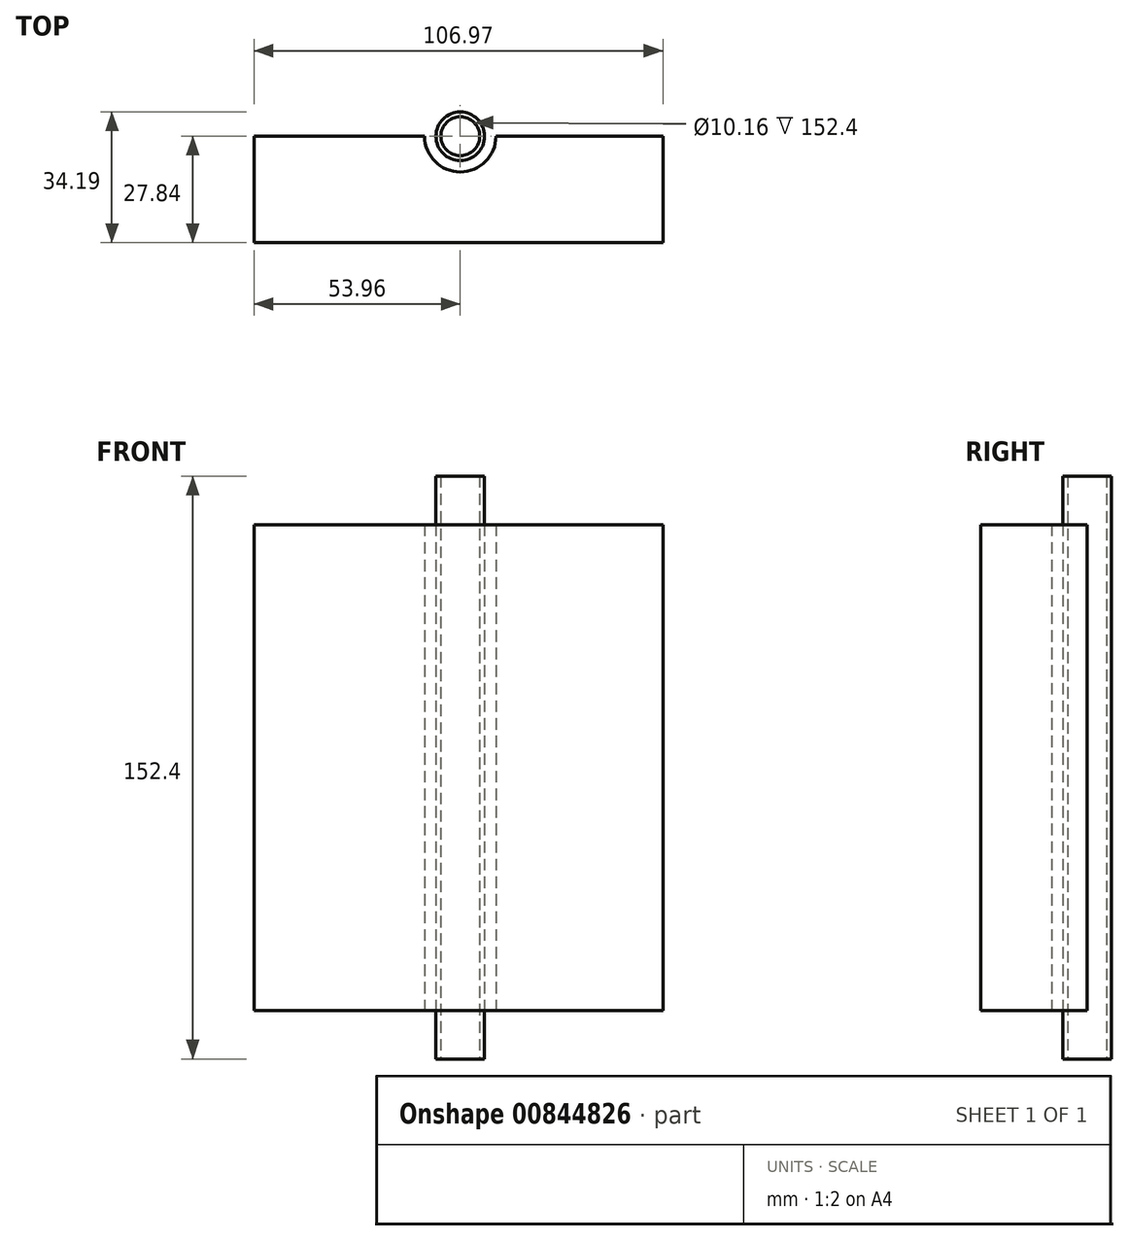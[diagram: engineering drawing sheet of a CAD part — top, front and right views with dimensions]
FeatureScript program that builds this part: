
annotation { "Feature Type Name" : "Feature", "Feature Type Description" : "" }
export const myFeature = defineFeature(function(context is Context, id is Id, definition is map)
    precondition{}
    {
        {
            var Q0;
            Q0=qCreatedBy(makeId("Top.planeOp"),FACE);
            var sketch = newSketch(context, id + "F0", { "sketchPlane" : qUnion([Q0])});
            skCircle(sketch, "E0", {"center": v(0, 0) * mm, "radius": 5.08 * mm});
            skCircle(sketch, "E1", {"center": v(0, 0) * mm, "radius": 6.35 * mm});
            skLineSegment(sketch, "E2.bottom", {"start": v(53.01, 0) * mm, "end": v(-53.96, 0) * mm});
            skLineSegment(sketch, "E2.top", {"start": v(53.01, -27.84) * mm, "end": v(-53.96, -27.84) * mm});
            skLineSegment(sketch, "E2.left", {"start": v(53.01, 0) * mm, "end": v(53.01, -27.84) * mm});
            skLineSegment(sketch, "E2.right", {"start": v(-53.96, 0) * mm, "end": v(-53.96, -27.84) * mm});
            skSolve(sketch);
        }
        {
            var Q0;
            Q0=makeQuery(id+"F0.imprint","IMPRINT",FACE,{"disambiguationData":[TD([[makeQuery(id+"F0.imprint","IMPRINT",EDGE,{"derivedFrom":sQuery(id+"F0.wireOp",EDGE,"E2.top")}),-1.0]])]});
            var sketch = newSketch(context, id + "F1", { "sketchPlane" : qUnion([Q0])});
            skCircle(sketch, "E3", {"center": v(0, 0) * mm, "radius": 9.33 * mm});
            skSolve(sketch);
        }
        {
            var Q0;
            Q0=makeQuery(id+"F1.imprint","IMPRINT",FACE,{"disambiguationData":[TD([[makeQuery(id+"F1.imprint","IMPRINT",EDGE,{"derivedFrom":makeQuery(id+"F0.imprint","IMPRINT",EDGE,{"derivedFrom":sQuery(id+"F0.wireOp",EDGE,"E2.top")})}),-1.0]])]});
            extrude(context, id + "F2", {"entities" : qUnion([Q0]), "endBound" : BoundingType.SYMMETRIC, "depth" : 127 * mm, "offsetDistance" : 25.4 * mm});
        }
        {
            var Q0;
            {var subQ0=sQuery(id+"F0.wireOp",EDGE,"E2.bottom");var subQ1=sQuery(id+"F0.wireOp",EDGE,"E0");var subQ2=makeQuery(id+"F0.imprint","INTERSECT",VERTEX,{"disambiguationData":[OD(0.0)],"derivedFrom":[subQ1,subQ0]});Q0=makeQuery(id+"F0.imprint","IMPRINT",FACE,{"disambiguationData":[TD([[makeQuery(id+"F0.imprint","IMPRINT",EDGE,{"disambiguationData":[TD([[subQ2,1.0]])],"derivedFrom":subQ1}),-1.0]])]});}
            var Q1;
            {var subQ0=sQuery(id+"F0.wireOp",EDGE,"E2.bottom");var subQ1=sQuery(id+"F0.wireOp",EDGE,"E0");var subQ2=makeQuery(id+"F0.imprint","INTERSECT",VERTEX,{"disambiguationData":[OD(0.0)],"derivedFrom":[subQ1,subQ0]});Q1=makeQuery(id+"F0.imprint","IMPRINT",FACE,{"disambiguationData":[TD([[makeQuery(id+"F0.imprint","IMPRINT",EDGE,{"disambiguationData":[TD([[subQ2,-1.0]])],"derivedFrom":subQ1}),-1.0]])]});}
            extrude(context, id + "F3", {"entities" : qUnion([Q0, Q1]), "endBound" : BoundingType.SYMMETRIC, "depth" : 152.4 * mm, "offsetDistance" : 25.4 * mm});
        }
    });
